# Revit family: Towel_Ring-Grohe-BauCosmopolitan-40460001
name_source: partatom
category: Specialty Equipment
units: mm (PartAtom-declared; Revit-internal decimal feet)

## family parameters
Cut with Voids When Loaded = No
Host = Face
OmniClass Number = 23.40.20.21.27
OmniClass Title = Towel Bars
Part Type = Normal
Room Calculation Point = No
Round Connector Dimension = Use Diameter
Shared = Yes

## types (1)
- 40460001
    Assembly Code = C1030200
    Default Elevation = 40"
    Description = BauCosmopolitan Towel ring
    Finish = Metal-Grohe-001-StarLight Chrome
    Height = 9 3/32"
    Installation Instruction Link = https://americanstandard.box.com
    Installation Type = Wall Mounted
    Length = 2 9/32"
    Manufacturer = Grohe
    Material = Metal-Grohe-001-StarLight Chrome
    Model = 40460001
    Price = Prices may vary. Please consult Manufacturer Representative for most up-to-date price list.
    Product Documentation Link = https://americanstandard.box.com
    Product Page URL = https://www.grohe.us
    Revised Date = 10/25/2021
    URL = https://www.grohe.us
    Width = 8 9/32"

## geometry (parser evidence)
native form markers: Sweep x5
no freeform markers — native parametric forms only
